# Revit family: Family Frame with Materials
name_source: partatom
category: Furniture Systems
revit_build: Autodesk Revit 2016 (Build: 20150220_1215(x64)
units: mm (PartAtom-declared; Revit-internal decimal feet)

## family parameters
Always vertical = Yes
Cut with Voids When Loaded = No
Part Type = Normal
Room Calculation Point = No
Round Connector Dimension = Use Diameter
Shared = No
Work Plane-Based = No

## types (1)
- Family Frame
    Ceiling = Mirror Ceiling
    Ceiling Height = 2980 mm
    Depth = 2000 mm  [stored 6.56168 ft]
    Floor = Wood Flooring
    Floor Thickness = 75 mm
    Frame Transoms = Aluminum 6061
    Frame Uprights = Steel, Mild
    Height = 3000 mm  [stored 9.84252 ft]
    Inner Depth = 1900 mm  [stored 6.2336 ft]
    Inner Width = 2900 mm  [stored 9.51444 ft]
    Rear Wall = <By Category>
    Width = 3000 mm  [stored 9.84252 ft]

note: [stored X ft] marks values corroborated as IEEE doubles in the binary element streams (Revit-internal decimal feet)

## geometry (parser evidence)
native form markers: Blend x4, Sweep x4
no freeform markers — native parametric forms only
